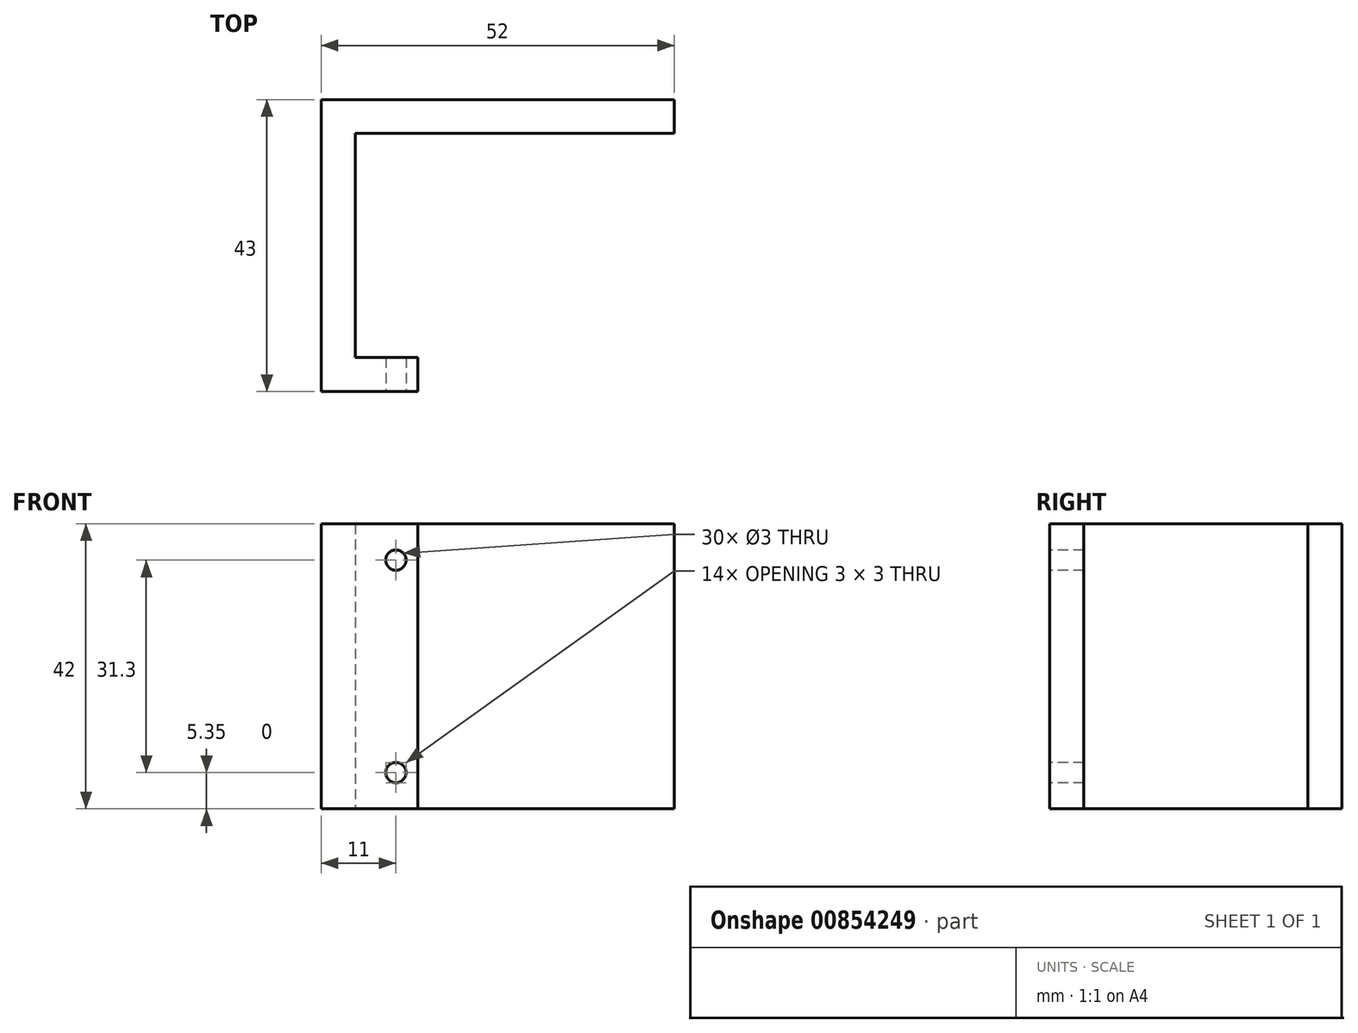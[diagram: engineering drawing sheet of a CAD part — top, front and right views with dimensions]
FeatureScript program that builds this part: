
annotation { "Feature Type Name" : "Feature", "Feature Type Description" : "" }
export const myFeature = defineFeature(function(context is Context, id is Id, definition is map)
    precondition{}
    {
        {
            var Q0;
            Q0=qCreatedBy(makeId("Top.planeOp"),FACE);
            var sketch = newSketch(context, id + "F0", { "sketchPlane" : qUnion([Q0])});
            skLineSegment(sketch, "E0.bottom", {"start": v(0, 9.35) * mm, "end": v(52, 9.35) * mm});
            skLineSegment(sketch, "E0.top", {"start": v(0, 14.35) * mm, "end": v(52, 14.35) * mm});
            skLineSegment(sketch, "E0.left", {"start": v(0, 9.35) * mm, "end": v(0, 14.35) * mm});
            skLineSegment(sketch, "E0.right", {"start": v(52, 9.35) * mm, "end": v(52, 14.35) * mm});
            skLineSegment(sketch, "E1.bottom", {"start": v(0, 9.35) * mm, "end": v(5, 9.35) * mm});
            skLineSegment(sketch, "E1.top", {"start": v(0, -28.65) * mm, "end": v(5, -28.65) * mm});
            skLineSegment(sketch, "E1.left", {"start": v(0, 9.35) * mm, "end": v(0, -28.65) * mm});
            skLineSegment(sketch, "E1.right", {"start": v(5, 9.35) * mm, "end": v(5, -28.65) * mm});
            skLineSegment(sketch, "E2.bottom", {"start": v(5, -28.65) * mm, "end": v(14.2, -28.65) * mm});
            skLineSegment(sketch, "E2.top", {"start": v(5, -23.65) * mm, "end": v(14.2, -23.65) * mm});
            skLineSegment(sketch, "E2.left", {"start": v(5, -28.65) * mm, "end": v(5, -23.65) * mm});
            skLineSegment(sketch, "E2.right", {"start": v(14.2, -28.65) * mm, "end": v(14.2, -23.65) * mm});
            skSolve(sketch);
        }
        {
            var Q0;
            Q0 = qSketchRegion(id + "F0", true);
            extrude(context, id + "F1", {"entities" : qUnion([Q0]), "depth" : 42 * mm, "offsetDistance" : 25 * mm});
        }
        {
            var Q0;
            Q0=makeQuery(id+"F1.opExtrude","SWEPT_FACE",FACE,{"disambiguationData":[OSD([sQuery(id+"F0.wireOp",EDGE,"E1.top"),sQuery(id+"F0.wireOp",EDGE,"E2.bottom")])]});
            var sketch = newSketch(context, id + "F2", { "sketchPlane" : qUnion([Q0])});
            skCircle(sketch, "E3", {"center": v(11, 36.65) * mm, "radius": 1.5 * mm});
            skLineSegment(sketch, "E4", {"start": v(0, 21) * mm, "end": v(52.02, 21) * mm, "construction": true});
            skCircle(sketch, "E5.MirrorC", {"center": v(11, 5.35) * mm, "radius": 1.5 * mm});
            skLineSegment(sketch, "E6", {"start": v(11, 36.65) * mm, "end": v(0, 36.65) * mm, "construction": true});
            skLineSegment(sketch, "E7", {"start": v(11, 36.65) * mm, "end": v(11, 42) * mm, "construction": true});
            skSolve(sketch);
        }
        {
            var Q0;
            Q0=sQuery(id+"F2.wireOp",VERTEX,"E3.center");
            var Q1;
            Q1=makeQuery(id+"F1.opExtrude","SWEPT_BODY",BODY,{"disambiguationData":[OSD([sQuery(id+"F0.wireOp",EDGE,"E0.bottom"),sQuery(id+"F0.wireOp",EDGE,"E0.top"),sQuery(id+"F0.wireOp",EDGE,"E0.left"),sQuery(id+"F0.wireOp",EDGE,"E0.right"),sQuery(id+"F0.wireOp",EDGE,"E1.top"),sQuery(id+"F0.wireOp",EDGE,"E1.left"),sQuery(id+"F0.wireOp",EDGE,"E1.right"),sQuery(id+"F0.wireOp",EDGE,"E2.bottom"),sQuery(id+"F0.wireOp",EDGE,"E2.top"),sQuery(id+"F0.wireOp",EDGE,"E2.right")])]});
            hole(context, id + "F3", {"style" : HoleStyle.SIMPLE, "endStyle" : HoleEndStyle.BLIND, "holeDiameter" : 3 * mm, "majorDiameter" : 5 * mm, "holeDepth" : 12 * mm, "isTappedThrough" : true, "tappedDepth" : 12 * mm, "tapClearance" : 3, "locations" : qUnion([Q0]), "scope" : qUnion([Q1])});
        }
        {
            var Q0;
            Q0=sQuery(id+"F2.wireOp",VERTEX,"E5.MirrorC.center");
            var Q1;
            Q1=makeQuery(id+"F1.opExtrude","SWEPT_BODY",BODY,{"disambiguationData":[OSD([sQuery(id+"F0.wireOp",EDGE,"E0.bottom"),sQuery(id+"F0.wireOp",EDGE,"E0.top"),sQuery(id+"F0.wireOp",EDGE,"E0.left"),sQuery(id+"F0.wireOp",EDGE,"E0.right"),sQuery(id+"F0.wireOp",EDGE,"E1.top"),sQuery(id+"F0.wireOp",EDGE,"E1.left"),sQuery(id+"F0.wireOp",EDGE,"E1.right"),sQuery(id+"F0.wireOp",EDGE,"E2.bottom"),sQuery(id+"F0.wireOp",EDGE,"E2.top"),sQuery(id+"F0.wireOp",EDGE,"E2.right")])]});
            hole(context, id + "F4", {"style" : HoleStyle.SIMPLE, "endStyle" : HoleEndStyle.BLIND, "holeDiameter" : 3 * mm, "majorDiameter" : 5 * mm, "holeDepth" : 12 * mm, "isTappedThrough" : true, "tappedDepth" : 12 * mm, "tapClearance" : 3, "locations" : qUnion([Q0]), "scope" : qUnion([Q1])});
        }
    });
